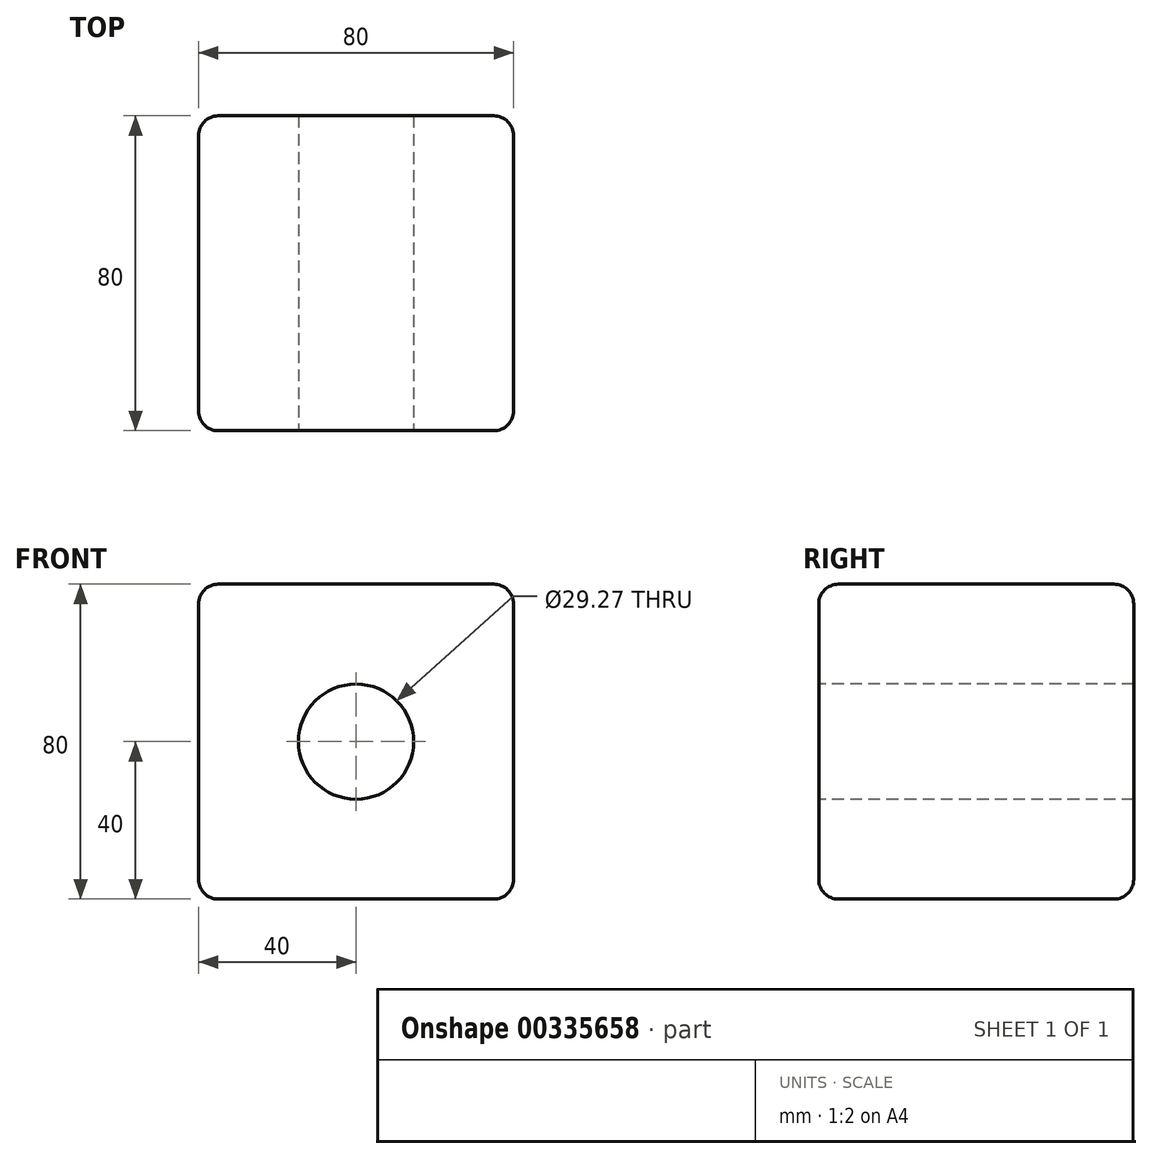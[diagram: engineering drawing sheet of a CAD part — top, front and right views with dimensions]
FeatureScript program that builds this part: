
annotation { "Feature Type Name" : "Feature", "Feature Type Description" : "" }
export const myFeature = defineFeature(function(context is Context, id is Id, definition is map)
    precondition{}
    {
        {
            var Q0;
            Q0=qCreatedBy(makeId("Top.planeOp"),FACE);
            var sketch = newSketch(context, id + "F0", { "sketchPlane" : qUnion([Q0])});
            skLineSegment(sketch, "E0.bottom", {"start": v(-40, 40) * mm, "end": v(40, 40) * mm});
            skLineSegment(sketch, "E0.top", {"start": v(-40, -40) * mm, "end": v(40, -40) * mm});
            skLineSegment(sketch, "E0.left", {"start": v(-40, 40) * mm, "end": v(-40, -40) * mm});
            skLineSegment(sketch, "E0.right", {"start": v(40, 40) * mm, "end": v(40, -40) * mm});
            skPoint(sketch, "E0.middle", {"position": v(0, 0) * mm});
            skSolve(sketch);
        }
        {
            var Q0;
            Q0=makeQuery(id+"F0.imprint","IMPRINT",FACE,{"disambiguationData":[TD([[makeQuery(id+"F0.imprint","IMPRINT",EDGE,{"derivedFrom":sQuery(id+"F0.wireOp",EDGE,"E0.bottom")}),-1.0]])]});
            extrude(context, id + "F1", {"entities" : qUnion([Q0]), "endBound" : BoundingType.SYMMETRIC, "depth" : 80 * mm});
        }
        {
            var Q0;
            Q0=makeQuery(id+"F1.opExtrude","SWEPT_EDGE",EDGE,{"disambiguationData":[OSD([sQuery(id+"F0.wireOp",EDGE,"E0.top"),sQuery(id+"F0.wireOp",EDGE,"E0.right")])]});
            var Q1;
            Q1=makeQuery(id+"F1.opExtrude","CAP_EDGE",EDGE,{"disambiguationData":[OSD([sQuery(id+"F0.wireOp",EDGE,"E0.top")])],"isStart":true});
            var Q2;
            Q2=makeQuery(id+"F1.opExtrude","SWEPT_EDGE",EDGE,{"disambiguationData":[OSD([sQuery(id+"F0.wireOp",EDGE,"E0.top"),sQuery(id+"F0.wireOp",EDGE,"E0.left")])]});
            var Q3;
            Q3=makeQuery(id+"F1.opExtrude","CAP_EDGE",EDGE,{"disambiguationData":[OSD([sQuery(id+"F0.wireOp",EDGE,"E0.left")])],"isStart":true});
            var Q4;
            Q4=makeQuery(id+"F1.opExtrude","CAP_EDGE",EDGE,{"disambiguationData":[OSD([sQuery(id+"F0.wireOp",EDGE,"E0.right")])],"isStart":true});
            var Q5;
            Q5=makeQuery(id+"F1.opExtrude","CAP_FACE",FACE,{"disambiguationData":[OSD([sQuery(id+"F0.wireOp",EDGE,"E0.bottom"),sQuery(id+"F0.wireOp",EDGE,"E0.top"),sQuery(id+"F0.wireOp",EDGE,"E0.left"),sQuery(id+"F0.wireOp",EDGE,"E0.right")])],"isStart":true});
            var Q6;
            Q6=makeQuery(id+"F1.opExtrude","SWEPT_EDGE",EDGE,{"disambiguationData":[OSD([sQuery(id+"F0.wireOp",EDGE,"E0.bottom"),sQuery(id+"F0.wireOp",EDGE,"E0.left")])]});
            var Q7;
            Q7=makeQuery(id+"F1.opExtrude","CAP_EDGE",EDGE,{"disambiguationData":[OSD([sQuery(id+"F0.wireOp",EDGE,"E0.left")])],"isStart":false});
            var Q8;
            Q8=makeQuery(id+"F1.opExtrude","CAP_EDGE",EDGE,{"disambiguationData":[OSD([sQuery(id+"F0.wireOp",EDGE,"E0.top")])],"isStart":false});
            var Q9;
            Q9=makeQuery(id+"F1.opExtrude","CAP_FACE",FACE,{"disambiguationData":[OSD([sQuery(id+"F0.wireOp",EDGE,"E0.bottom"),sQuery(id+"F0.wireOp",EDGE,"E0.top"),sQuery(id+"F0.wireOp",EDGE,"E0.left"),sQuery(id+"F0.wireOp",EDGE,"E0.right")])],"isStart":false});
            var Q10;
            Q10=makeQuery(id+"F1.opExtrude","SWEPT_EDGE",EDGE,{"disambiguationData":[OSD([sQuery(id+"F0.wireOp",EDGE,"E0.bottom"),sQuery(id+"F0.wireOp",EDGE,"E0.right")])]});
            var Q11;
            Q11=makeQuery(id+"F1.opExtrude","CAP_EDGE",EDGE,{"disambiguationData":[OSD([sQuery(id+"F0.wireOp",EDGE,"E0.right")])],"isStart":false});
            fillet(context, id + "F2", {"entities" : qUnion([Q0, Q1, Q2, Q3, Q4, Q5, Q6, Q7, Q8, Q9, Q10, Q11]), "radius" : 5 * mm, "tangentPropagation" : true, "allowEdgeOverflow" : false});
        }
        {
            var Q0;
            Q0=makeQuery(id+"F1.opExtrude","SWEPT_FACE",FACE,{"disambiguationData":[OSD([sQuery(id+"F0.wireOp",EDGE,"E0.top")])]});
            var sketch = newSketch(context, id + "F3", { "sketchPlane" : qUnion([Q0])});
            skCircle(sketch, "E1", {"center": v(0, 0) * mm, "radius": 14.64 * mm});
            skSolve(sketch);
        }
        {
            var Q0;
            Q0 = qSketchRegion(id + "F3", true);
            extrude(context, id + "F4", {"entities" : qUnion([Q0]), "operationType" : NewBodyOperationType.REMOVE, "endBound" : BoundingType.THROUGH_ALL, "oppositeDirection" : true, "depth" : 25 * mm});
        }
    });
